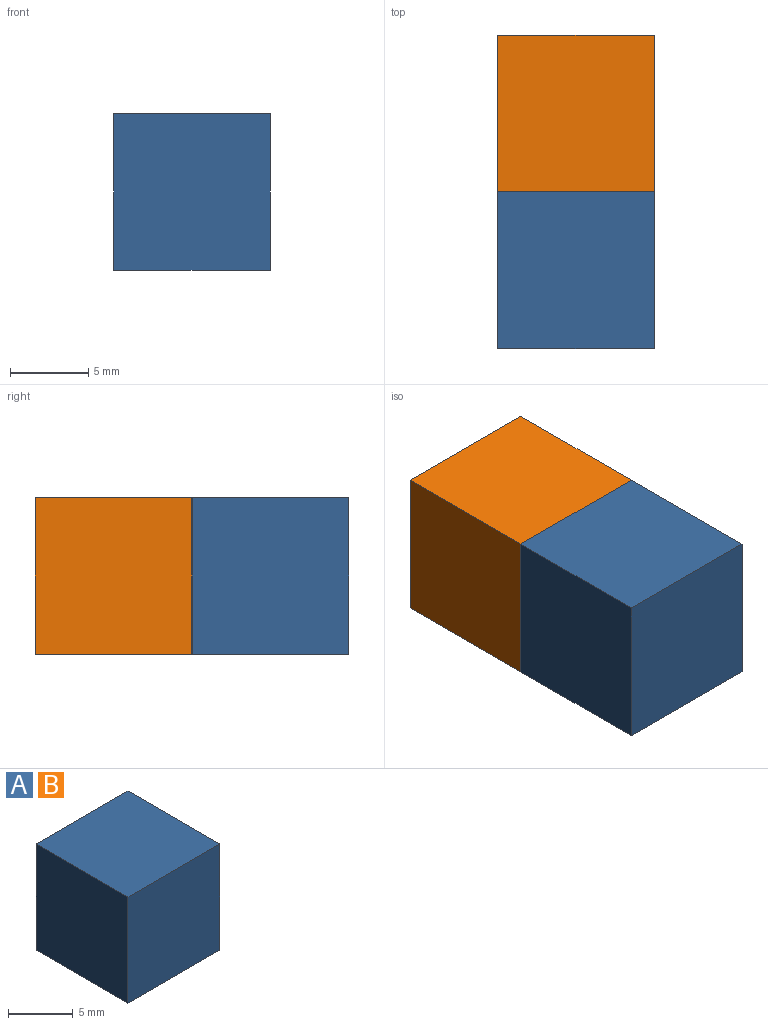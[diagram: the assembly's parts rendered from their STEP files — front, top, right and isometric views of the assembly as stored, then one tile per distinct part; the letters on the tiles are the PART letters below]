
ASSEMBLY  parts=2 mates=2
PART A: 6 faces, bbox 10x10x10 mm
  f0: plane 10x10mm, normal (0,-1,0), area 100mm2, adj f1,f3,f4,f5
  f1: plane 10x10mm, normal (1,0,0), area 100mm2, adj f0,f2,f4,f5
  f2: plane 10x10mm, normal (0,1,0), area 100mm2, adj f1,f3,f4,f5
  f3: plane 10x10mm, normal (-1,0,0), area 100mm2, adj f0,f2,f4,f5
  f4: plane 10x10mm, normal (0,0,1), area 100mm2, adj f0,f1,f2,f3
  f5: plane 10x10mm, normal (0,0,-1), area 100mm2, adj f0,f1,f2,f3
PART B: same geometry as A
PLACE A rot(axis=(-0.58,0.58,-0.58),120deg) t=(-35.48,-5.73,11.32)mm
PLACE B t=(-30.48,4.27,6.32)mm
MATE fastened B.f3 <-> B.f0  axis (-1,0,0) through (-35.48,4.27,11.32)mm
MATE fastened B.f0 <-> A.f3  axis (0,-1,0) through (-30.48,-0.73,11.32)mm
